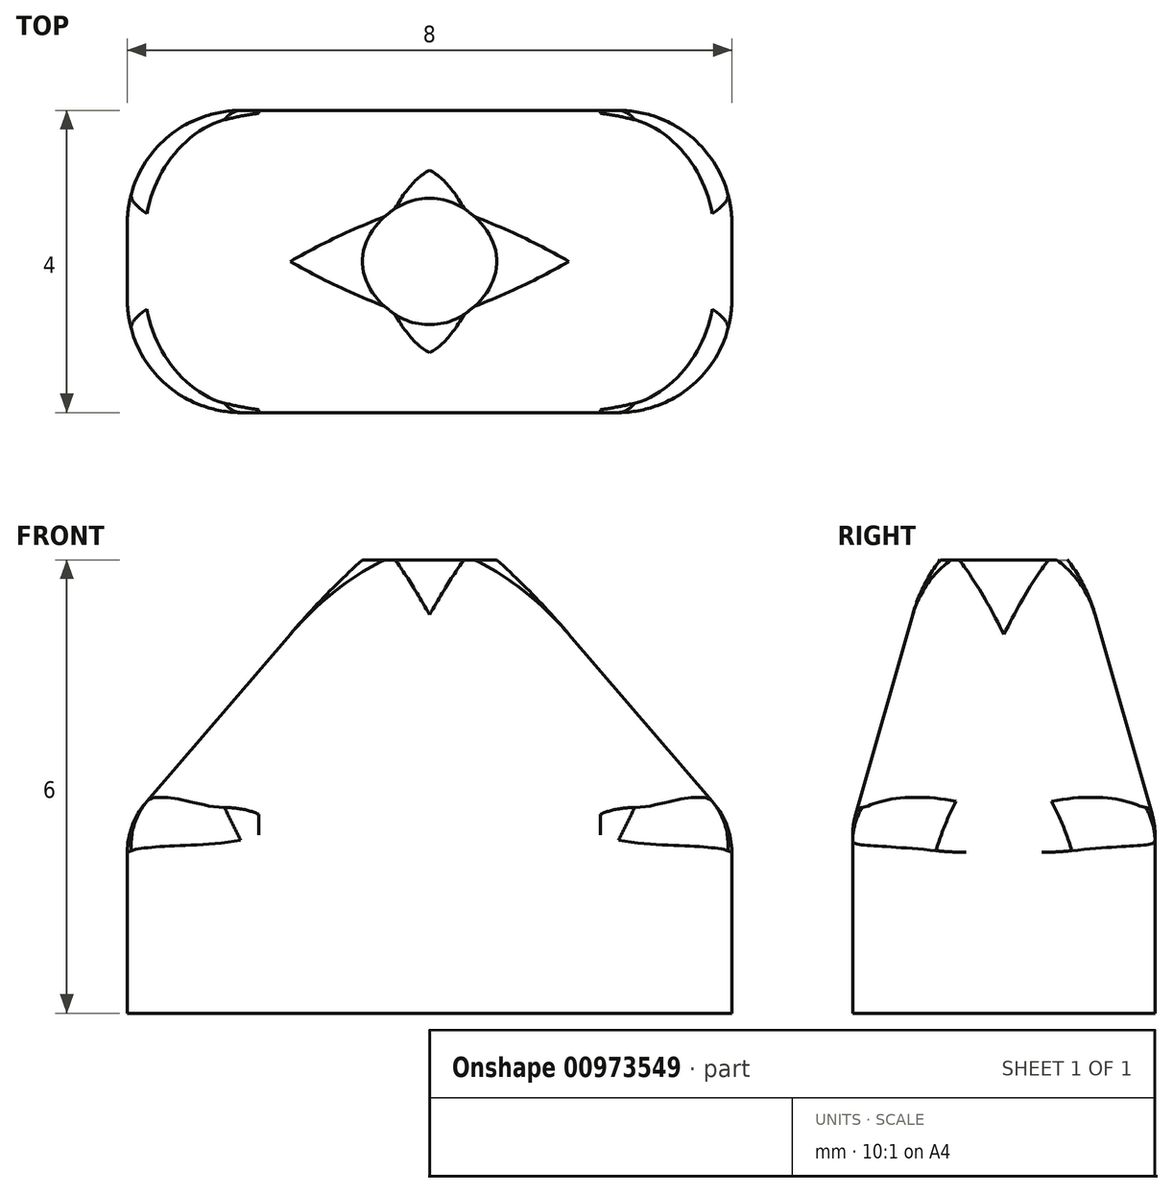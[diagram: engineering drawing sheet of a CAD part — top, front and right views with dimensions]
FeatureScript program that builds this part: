
annotation { "Feature Type Name" : "Feature", "Feature Type Description" : "" }
export const myFeature = defineFeature(function(context is Context, id is Id, definition is map)
    precondition{}
    {
        {
            var Q0;
            Q0=qCreatedBy(makeId("Top.planeOp"),FACE);
            var sketch = newSketch(context, id + "F0", { "sketchPlane" : qUnion([Q0])});
            skLineSegment(sketch, "E0.bottom", {"start": v(0, 0) * mm, "end": v(8, 0) * mm});
            skLineSegment(sketch, "E0.top", {"start": v(0, 4) * mm, "end": v(8, 4) * mm});
            skLineSegment(sketch, "E0.left", {"start": v(0, 0) * mm, "end": v(0, 4) * mm});
            skLineSegment(sketch, "E0.right", {"start": v(8, 0) * mm, "end": v(8, 4) * mm});
            skSolve(sketch);
        }
        {
            var Q0;
            Q0=makeQuery(id+"F0.imprint","IMPRINT",FACE,{"disambiguationData":[TD([[makeQuery(id+"F0.imprint","IMPRINT",EDGE,{"derivedFrom":sQuery(id+"F0.wireOp",EDGE,"E0.bottom")}),1.0]])]});
            extrude(context, id + "F1", {"entities" : qUnion([Q0]), "depth" : 6 * mm, "offsetDistance" : 25 * mm});
        }
        {
            var Q0;
            Q0=makeQuery(id+"F1.opExtrude","SWEPT_FACE",FACE,{"disambiguationData":[OSD([sQuery(id+"F0.wireOp",EDGE,"E0.bottom")])]});
            var sketch = newSketch(context, id + "F2", { "sketchPlane" : qUnion([Q0])});
            skLineSegment(sketch, "E1.0.0", {"start": v(0, 0) * mm, "end": v(8, 0) * mm});
            skLineSegment(sketch, "E1.0.1", {"start": v(8, 0) * mm, "end": v(8, 6) * mm});
            skLineSegment(sketch, "E1.0.2", {"start": v(8, 6) * mm, "end": v(0, 6) * mm});
            skLineSegment(sketch, "E1.0.3", {"start": v(0, 6) * mm, "end": v(0, 0) * mm});
            skLineSegment(sketch, "E2", {"start": v(0, 2.5) * mm, "end": v(3, 6) * mm});
            skLineSegment(sketch, "E3", {"start": v(5, 6) * mm, "end": v(8, 2.5) * mm});
            skPoint(sketch, "E4", {"position": v(4, 6) * mm});
            skSolve(sketch);
        }
        {
            var Q0;
            {var subQ3=sQuery(id+"F2.wireOp",EDGE,"E2");Q0=makeQuery(id+"F2.imprint","IMPRINT",FACE,{"disambiguationData":[TD([[makeQuery(id+"F2.imprint","IMPRINT",EDGE,{"derivedFrom":subQ3}),1.0]])]});}
            var Q1;
            {var subQ3=sQuery(id+"F2.wireOp",EDGE,"E3");Q1=makeQuery(id+"F2.imprint","IMPRINT",FACE,{"disambiguationData":[TD([[makeQuery(id+"F2.imprint","IMPRINT",EDGE,{"derivedFrom":subQ3}),1.0]])]});}
            extrude(context, id + "F3", {"entities" : qUnion([Q0, Q1]), "operationType" : NewBodyOperationType.REMOVE, "oppositeDirection" : true, "depth" : 25 * mm, "offsetDistance" : 25 * mm});
        }
        {
            var Q0;
            Q0=makeQuery(id+"F1.opExtrude","SWEPT_FACE",FACE,{"disambiguationData":[OSD([sQuery(id+"F0.wireOp",EDGE,"E0.left")])]});
            var sketch = newSketch(context, id + "F4", { "sketchPlane" : qUnion([Q0])});
            skLineSegment(sketch, "E5.0.0", {"start": v(-4, 6) * mm, "end": v(-4, 2.5) * mm});
            skLineSegment(sketch, "E5.0.1", {"start": v(-4, 2.5) * mm, "end": v(0, 2.5) * mm});
            skLineSegment(sketch, "E5.0.2", {"start": v(0, 2.5) * mm, "end": v(0, 6) * mm});
            skLineSegment(sketch, "E5.0.3", {"start": v(0, 6) * mm, "end": v(-4, 6) * mm});
            skLineSegment(sketch, "E6.0.0", {"start": v(0, 2.5) * mm, "end": v(-4, 2.5) * mm});
            skLineSegment(sketch, "E6.0.1", {"start": v(-4, 2.5) * mm, "end": v(-4, 0) * mm});
            skLineSegment(sketch, "E6.0.2", {"start": v(-4, 0) * mm, "end": v(0, 0) * mm});
            skLineSegment(sketch, "E6.0.3", {"start": v(0, 0) * mm, "end": v(0, 2.5) * mm});
            skLineSegment(sketch, "E7", {"start": v(-4, 2.5) * mm, "end": v(-3, 6) * mm});
            skLineSegment(sketch, "E8", {"start": v(0, 2.5) * mm, "end": v(-1, 6) * mm});
            skSolve(sketch);
        }
        {
            var Q0;
            {var subQ0=sQuery(id+"F4.wireOp",EDGE,"E5.0.0");Q0=makeQuery(id+"F4.imprint","IMPRINT",FACE,{"disambiguationData":[TD([[makeQuery(id+"F4.imprint","IMPRINT",EDGE,{"derivedFrom":subQ0}),1.0]])]});}
            var Q1;
            {var subQ0=sQuery(id+"F4.wireOp",EDGE,"E5.0.2");Q1=makeQuery(id+"F4.imprint","IMPRINT",FACE,{"disambiguationData":[TD([[makeQuery(id+"F4.imprint","IMPRINT",EDGE,{"derivedFrom":subQ0}),1.0]])]});}
            extrude(context, id + "F5", {"entities" : qUnion([Q0, Q1]), "operationType" : NewBodyOperationType.REMOVE, "oppositeDirection" : true, "depth" : 25 * mm, "offsetDistance" : 25 * mm});
        }
        {
            var Q0;
            Q0=makeQuery(id+"F5.boolean.opBoolean","INTERSECT",EDGE,{"derivedFrom":[makeQuery(id+"F3.boolean.opBoolean","COPY",FACE,{"derivedFrom":makeQuery(id+"F3.opExtrude","SWEPT_FACE",FACE,{"disambiguationData":[OSD([sQuery(id+"F2.wireOp",EDGE,"E2")])]})}),makeQuery(id+"F5.opExtrude","SWEPT_FACE",FACE,{"disambiguationData":[OSD([sQuery(id+"F4.wireOp",EDGE,"E7")])]})]});
            var Q1;
            Q1=makeQuery(id+"F5.boolean.opBoolean","INTERSECT",EDGE,{"derivedFrom":[makeQuery(id+"F3.boolean.opBoolean","COPY",FACE,{"derivedFrom":makeQuery(id+"F3.opExtrude","SWEPT_FACE",FACE,{"disambiguationData":[OSD([sQuery(id+"F2.wireOp",EDGE,"E2")])]})}),makeQuery(id+"F5.opExtrude","SWEPT_FACE",FACE,{"disambiguationData":[OSD([sQuery(id+"F4.wireOp",EDGE,"E8")])]})]});
            var Q2;
            Q2=makeQuery(id+"F5.boolean.opBoolean","INTERSECT",EDGE,{"derivedFrom":[makeQuery(id+"F3.boolean.opBoolean","COPY",FACE,{"derivedFrom":makeQuery(id+"F3.opExtrude","SWEPT_FACE",FACE,{"disambiguationData":[OSD([sQuery(id+"F2.wireOp",EDGE,"E3")])]})}),makeQuery(id+"F5.opExtrude","SWEPT_FACE",FACE,{"disambiguationData":[OSD([sQuery(id+"F4.wireOp",EDGE,"E8")])]})]});
            var Q3;
            Q3=makeQuery(id+"F5.boolean.opBoolean","INTERSECT",EDGE,{"derivedFrom":[makeQuery(id+"F3.boolean.opBoolean","COPY",FACE,{"derivedFrom":makeQuery(id+"F3.opExtrude","SWEPT_FACE",FACE,{"disambiguationData":[OSD([sQuery(id+"F2.wireOp",EDGE,"E3")])]})}),makeQuery(id+"F5.opExtrude","SWEPT_FACE",FACE,{"disambiguationData":[OSD([sQuery(id+"F4.wireOp",EDGE,"E7")])]})]});
            var Q4;
            Q4=makeQuery(id+"F1.opExtrude","SWEPT_EDGE",EDGE,{"disambiguationData":[OSD([sQuery(id+"F0.wireOp",EDGE,"E0.bottom"),sQuery(id+"F0.wireOp",EDGE,"E0.right")])]});
            var Q5;
            Q5=makeQuery(id+"F1.opExtrude","SWEPT_EDGE",EDGE,{"disambiguationData":[OSD([sQuery(id+"F0.wireOp",EDGE,"E0.top"),sQuery(id+"F0.wireOp",EDGE,"E0.right")])]});
            var Q6;
            Q6=makeQuery(id+"F1.opExtrude","SWEPT_EDGE",EDGE,{"disambiguationData":[OSD([sQuery(id+"F0.wireOp",EDGE,"E0.top"),sQuery(id+"F0.wireOp",EDGE,"E0.left")])]});
            var Q7;
            Q7=makeQuery(id+"F1.opExtrude","SWEPT_EDGE",EDGE,{"disambiguationData":[OSD([sQuery(id+"F0.wireOp",EDGE,"E0.bottom"),sQuery(id+"F0.wireOp",EDGE,"E0.left")])]});
            fillet(context, id + "F6", {"entities" : qUnion([Q0, Q1, Q2, Q3, Q4, Q5, Q6, Q7]), "radius" : 1.5 * mm, "tangentPropagation" : true, "allowEdgeOverflow" : false});
        }
        {
            var Q0;
            {var subQ0=makeQuery(id+"F5.opExtrude","SWEPT_FACE",FACE,{"disambiguationData":[OSD([sQuery(id+"F4.wireOp",EDGE,"E7")])]});Q0=makeQuery(id+"F6.opFillet","BLEND_EDGE",EDGE,{"blendedFrom":[makeQuery(id+"F5.boolean.opBoolean","INTERSECT",EDGE,{"derivedFrom":[makeQuery(id+"F3.boolean.opBoolean","COPY",FACE,{"derivedFrom":makeQuery(id+"F3.opExtrude","SWEPT_FACE",FACE,{"disambiguationData":[OSD([sQuery(id+"F2.wireOp",EDGE,"E2")])]})}),subQ0]}),makeQuery(id+"F5.boolean.opBoolean","INTERSECT",EDGE,{"derivedFrom":[makeQuery(id+"F3.boolean.opBoolean","COPY",FACE,{"derivedFrom":makeQuery(id+"F3.opExtrude","SWEPT_FACE",FACE,{"disambiguationData":[OSD([sQuery(id+"F2.wireOp",EDGE,"E3")])]})}),subQ0]})],"blendedInto":[]});}
            var Q1;
            {var subQ0=makeQuery(id+"F3.boolean.opBoolean","COPY",FACE,{"derivedFrom":makeQuery(id+"F3.opExtrude","SWEPT_FACE",FACE,{"disambiguationData":[OSD([sQuery(id+"F2.wireOp",EDGE,"E2")])]})});Q1=makeQuery(id+"F6.opFillet","BLEND_EDGE",EDGE,{"blendedFrom":[makeQuery(id+"F5.boolean.opBoolean","INTERSECT",EDGE,{"derivedFrom":[subQ0,makeQuery(id+"F5.opExtrude","SWEPT_FACE",FACE,{"disambiguationData":[OSD([sQuery(id+"F4.wireOp",EDGE,"E8")])]})]}),makeQuery(id+"F5.boolean.opBoolean","INTERSECT",EDGE,{"derivedFrom":[subQ0,makeQuery(id+"F5.opExtrude","SWEPT_FACE",FACE,{"disambiguationData":[OSD([sQuery(id+"F4.wireOp",EDGE,"E7")])]})]})],"blendedInto":[]});}
            var Q2;
            {var subQ0=makeQuery(id+"F5.opExtrude","SWEPT_FACE",FACE,{"disambiguationData":[OSD([sQuery(id+"F4.wireOp",EDGE,"E8")])]});Q2=makeQuery(id+"F6.opFillet","BLEND_EDGE",EDGE,{"blendedFrom":[makeQuery(id+"F5.boolean.opBoolean","INTERSECT",EDGE,{"derivedFrom":[makeQuery(id+"F3.boolean.opBoolean","COPY",FACE,{"derivedFrom":makeQuery(id+"F3.opExtrude","SWEPT_FACE",FACE,{"disambiguationData":[OSD([sQuery(id+"F2.wireOp",EDGE,"E2")])]})}),subQ0]}),makeQuery(id+"F5.boolean.opBoolean","INTERSECT",EDGE,{"derivedFrom":[makeQuery(id+"F3.boolean.opBoolean","COPY",FACE,{"derivedFrom":makeQuery(id+"F3.opExtrude","SWEPT_FACE",FACE,{"disambiguationData":[OSD([sQuery(id+"F2.wireOp",EDGE,"E3")])]})}),subQ0]})],"blendedInto":[]});}
            var Q3;
            {var subQ0=makeQuery(id+"F3.boolean.opBoolean","COPY",FACE,{"derivedFrom":makeQuery(id+"F3.opExtrude","SWEPT_FACE",FACE,{"disambiguationData":[OSD([sQuery(id+"F2.wireOp",EDGE,"E3")])]})});Q3=makeQuery(id+"F6.opFillet","BLEND_EDGE",EDGE,{"blendedFrom":[makeQuery(id+"F5.boolean.opBoolean","INTERSECT",EDGE,{"derivedFrom":[subQ0,makeQuery(id+"F5.opExtrude","SWEPT_FACE",FACE,{"disambiguationData":[OSD([sQuery(id+"F4.wireOp",EDGE,"E8")])]})]}),makeQuery(id+"F5.boolean.opBoolean","INTERSECT",EDGE,{"derivedFrom":[subQ0,makeQuery(id+"F5.opExtrude","SWEPT_FACE",FACE,{"disambiguationData":[OSD([sQuery(id+"F4.wireOp",EDGE,"E7")])]})]})],"blendedInto":[]});}
            var Q4;
            Q4=makeQuery(id+"F5.boolean.opBoolean","COPY",EDGE,{"derivedFrom":makeQuery(id+"F5.opExtrude","SWEPT_EDGE",EDGE,{"disambiguationData":[OSD([sQuery(id+"F4.wireOp",EDGE,"E5.0.2"),sQuery(id+"F4.wireOp",EDGE,"E6.0.0"),sQuery(id+"F4.wireOp",EDGE,"E6.0.3"),sQuery(id+"F4.wireOp",EDGE,"E8")])]})});
            var Q5;
            Q5=makeQuery(id+"F3.boolean.opBoolean","COPY",EDGE,{"derivedFrom":makeQuery(id+"F3.opExtrude","SWEPT_EDGE",EDGE,{"disambiguationData":[OSD([sQuery(id+"F2.wireOp",EDGE,"E1.0.1"),sQuery(id+"F2.wireOp",EDGE,"E3")])]})});
            var Q6;
            Q6=makeQuery(id+"F6.opFillet","BLEND_EDGE",EDGE,{"blendedFrom":[makeQuery(id+"F1.opExtrude","SWEPT_EDGE",EDGE,{"disambiguationData":[OSD([sQuery(id+"F0.wireOp",EDGE,"E0.bottom"),sQuery(id+"F0.wireOp",EDGE,"E0.right")])]}),makeQuery(id+"F5.boolean.opBoolean","INTERSECT",EDGE,{"derivedFrom":[makeQuery(id+"F3.boolean.opBoolean","COPY",FACE,{"derivedFrom":makeQuery(id+"F3.opExtrude","SWEPT_FACE",FACE,{"disambiguationData":[OSD([sQuery(id+"F2.wireOp",EDGE,"E3")])]})}),makeQuery(id+"F5.opExtrude","SWEPT_FACE",FACE,{"disambiguationData":[OSD([sQuery(id+"F4.wireOp",EDGE,"E8")])]})]})],"blendedInto":[]});
            fillet(context, id + "F7", {"entities" : qUnion([Q0, Q1, Q2, Q3, Q4, Q5, Q6]), "radius" : 1 * mm, "tangentPropagation" : true, "allowEdgeOverflow" : false});
        }
    });
